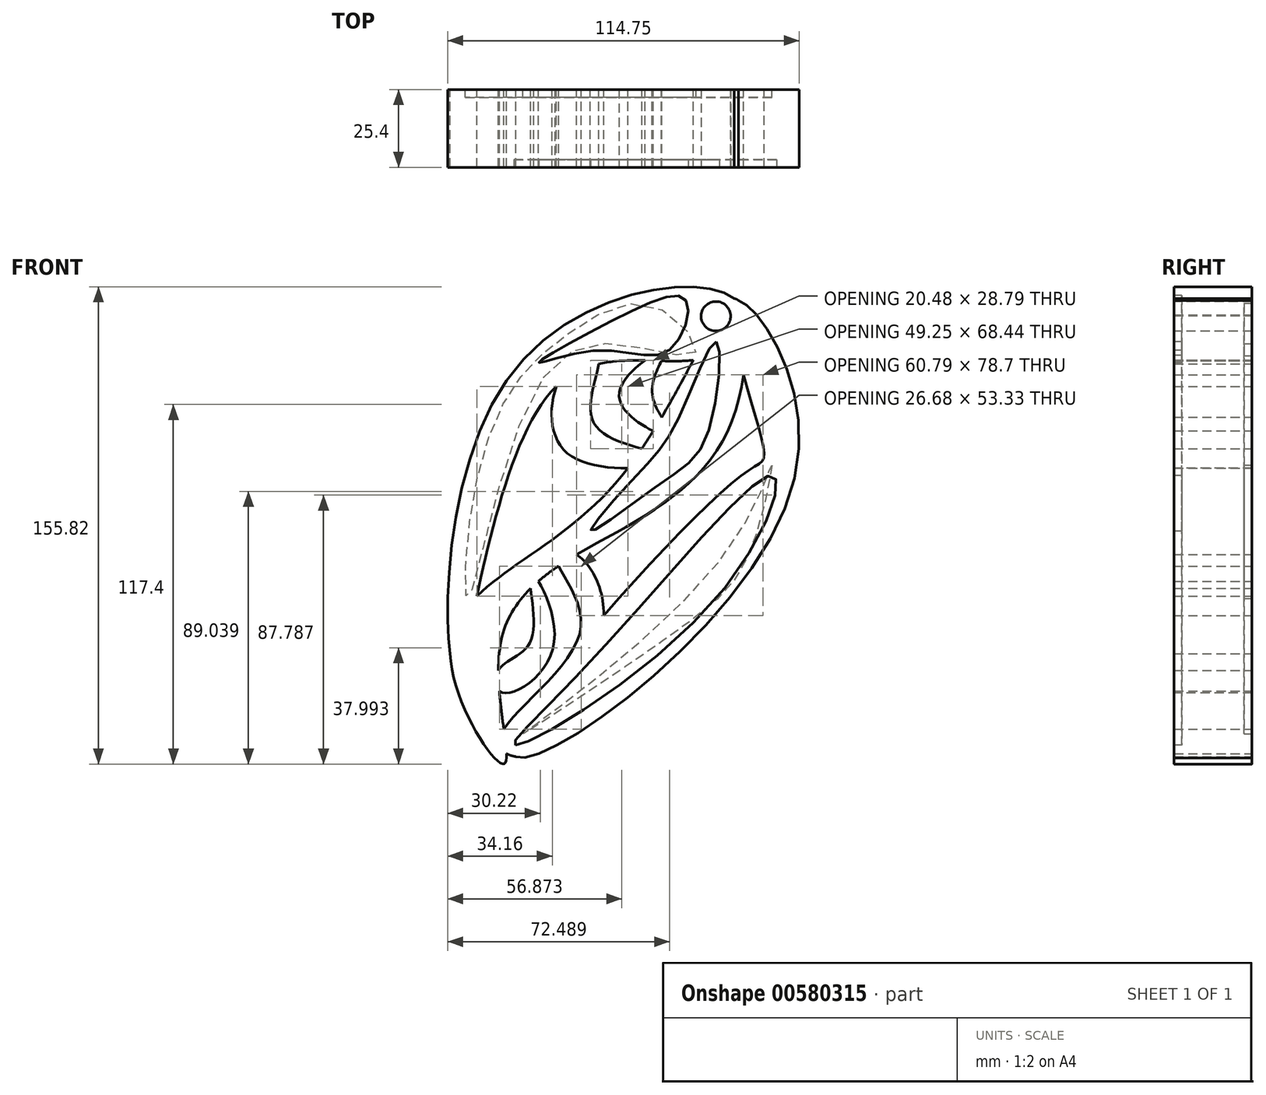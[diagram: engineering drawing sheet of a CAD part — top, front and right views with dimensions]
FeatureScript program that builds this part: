
annotation { "Feature Type Name" : "Feature", "Feature Type Description" : "" }
export const myFeature = defineFeature(function(context is Context, id is Id, definition is map)
    precondition{}
    {
        {
            var Q0;
            Q0=qCreatedBy(makeId("Front.planeOp"),FACE);
            var sketch = newSketch(context, id + "F0", { "sketchPlane" : qUnion([Q0])});
            skFitSpline(sketch, "E0", {"points": [v(37.9, 75.8) * mm, v(37.6, 37.9) * mm, v(0, 0) * mm, v(-38.5, -35.8) * mm, v(-37.6, -76.1) * mm, v(-55.04, -37.9) * mm, v(-3, 13.54) * mm, v(37.9, 75.8) * mm]});
            skSolve(sketch);
        }
        {
            var Q0;
            Q0 = qSketchRegion(id + "F0", true);
            extrude(context, id + "F1", {"entities" : qUnion([Q0]), "depth" : 25.4 * mm, "offsetDistance" : 25.4 * mm});
        }
        {
            var Q0;
            Q0=qCreatedBy(makeId("Front.planeOp"),FACE);
            var sketch = newSketch(context, id + "F2", { "sketchPlane" : qUnion([Q0])});
            skFitSpline(sketch, "E1", {"points": [v(-39.1, -45.12) * mm, v(-28.57, -35.2) * mm, v(-28.88, -14.14) * mm, v(-21.36, -37.3) * mm, v(-38.5, -52.64) * mm, v(-39.1, -45.12) * mm]});
            skSolve(sketch);
        }
        {
            var Q0;
            Q0 = qSketchRegion(id + "F2", true);
            extrude(context, id + "F3", {"entities" : qUnion([Q0]), "operationType" : NewBodyOperationType.ADD, "depth" : 25.4 * mm, "offsetDistance" : 25.4 * mm});
        }
        {
            var Q0;
            Q0=qCreatedBy(makeId("Front.planeOp"),FACE);
            var sketch = newSketch(context, id + "F4", { "sketchPlane" : qUnion([Q0])});
            skFitSpline(sketch, "E2", {"points": [v(-20.75, -8.42) * mm, v(-12.63, -32.49) * mm, v(-39.1, -68.58) * mm, v(-27.37, -72.8) * mm, v(-5.11, -24.66) * mm, v(-17.15, -6.32) * mm, v(-20.75, -8.42) * mm]});
            skSolve(sketch);
        }
        {
            var Q0;
            Q0 = qSketchRegion(id + "F4", true);
            extrude(context, id + "F5", {"entities" : qUnion([Q0]), "operationType" : NewBodyOperationType.ADD, "depth" : 25.4 * mm, "offsetDistance" : 25.4 * mm});
        }
        {
            var Q0;
            Q0=qCreatedBy(makeId("Front.planeOp"),FACE);
            var sketch = newSketch(context, id + "F6", { "sketchPlane" : qUnion([Q0])});
            skFitSpline(sketch, "E3", {"points": [v(38.8, 74.6) * mm, v(-35.5, 50.83) * mm, v(-52.94, -44.82) * mm, v(-21.06, 46.62) * mm, v(30.08, 57.15) * mm, v(38.8, 74.6) * mm]});
            skSolve(sketch);
        }
        {
            var Q0;
            Q0 = qSketchRegion(id + "F6", true);
            extrude(context, id + "F7", {"entities" : qUnion([Q0]), "operationType" : NewBodyOperationType.ADD, "depth" : 25.4 * mm, "offsetDistance" : 25.4 * mm});
        }
        {
            var Q0;
            Q0=qCreatedBy(makeId("Front.planeOp"),FACE);
            var sketch = newSketch(context, id + "F8", { "sketchPlane" : qUnion([Q0])});
            skCircle(sketch, "E4", {"center": v(30.98, 69.78) * mm, "radius": 4.44 * mm});
            skSolve(sketch);
        }
        {
            var Q0;
            Q0 = qSketchRegion(id + "F8", true);
            extrude(context, id + "F9", {"entities" : qUnion([Q0]), "operationType" : NewBodyOperationType.REMOVE, "oppositeDirection" : true, "depth" : 25.4 * mm, "offsetDistance" : 25.4 * mm});
        }
        {
            var Q0;
            Q0=makeQuery(id+"F7.boolean.opBoolean","MERGE",FACE,{"derivedFrom":[makeQuery(id+"F5.boolean.opBoolean","MERGE",FACE,{"derivedFrom":[makeQuery(id+"F3.boolean.opBoolean","MERGE",FACE,{"derivedFrom":[makeQuery(id+"F1.opExtrude","CAP_FACE",FACE,{"disambiguationData":[OSD([sQuery(id+"F0.wireOp",EDGE,"E0")])],"isStart":false}),makeQuery(id+"F3.opExtrude","CAP_FACE",FACE,{"disambiguationData":[OSD([sQuery(id+"F2.wireOp",EDGE,"E1")])],"isStart":false})]}),makeQuery(id+"F5.opExtrude","CAP_FACE",FACE,{"disambiguationData":[OSD([sQuery(id+"F4.wireOp",EDGE,"E2")])],"isStart":false})]}),makeQuery(id+"F7.opExtrude","CAP_FACE",FACE,{"disambiguationData":[OSD([sQuery(id+"F6.wireOp",EDGE,"E3")])],"isStart":false})]});
            var sketch = newSketch(context, id + "F10", { "sketchPlane" : qUnion([Q0])});
            skCircle(sketch, "E5", {"center": v(31.58, 70.08) * mm, "radius": 4.82 * mm});
            skSolve(sketch);
        }
        {
            var Q0;
            Q0 = qSketchRegion(id + "F10", true);
            extrude(context, id + "F11", {"entities" : qUnion([Q0]), "operationType" : NewBodyOperationType.REMOVE, "oppositeDirection" : true, "depth" : 25.4 * mm, "offsetDistance" : 25.4 * mm});
        }
        {
            var Q0;
            Q0=qCreatedBy(makeId("Front.planeOp"),FACE);
            var sketch = newSketch(context, id + "F12", { "sketchPlane" : qUnion([Q0])});
            skFitSpline(sketch, "E6", {"points": [v(37, 74.6) * mm, v(57.45, 18.05) * mm, v(-34.6, -72.8) * mm, v(40.6, 18.65) * mm, v(47.22, 26.17) * mm, v(37, 74.6) * mm]});
            skSolve(sketch);
        }
        {
            var Q0;
            Q0 = qSketchRegion(id + "F12", true);
            extrude(context, id + "F13", {"entities" : qUnion([Q0]), "operationType" : NewBodyOperationType.ADD, "depth" : 25.4 * mm, "offsetDistance" : 25.4 * mm});
        }
        {
            var Q0;
            Q0=qCreatedBy(makeId("Front.planeOp"),FACE);
            var sketch = newSketch(context, id + "F14", { "sketchPlane" : qUnion([Q0])});
            skFitSpline(sketch, "E7", {"points": [v(14.15, 58.06) * mm, v(10.77, 45.14) * mm, v(16.62, 31.3) * mm, v(0, 43.9) * mm, v(14.15, 58.06) * mm]});
            skSolve(sketch);
        }
        {
            var Q0;
            Q0 = qSketchRegion(id + "F14", true);
            extrude(context, id + "F15", {"entities" : qUnion([Q0]), "operationType" : NewBodyOperationType.ADD, "depth" : 25.4 * mm, "offsetDistance" : 25.4 * mm});
        }
        {
            var Q0;
            Q0=qCreatedBy(makeId("Front.planeOp"),FACE);
            var sketch = newSketch(context, id + "F16", { "sketchPlane" : qUnion([Q0])});
            skFitSpline(sketch, "E8", {"points": [v(-6.77, 57.14) * mm, v(-7.7, 34.37) * mm, v(17.23, 23.6) * mm, v(-16.62, 25.14) * mm, v(-15.08, 56.52) * mm, v(-6.77, 57.14) * mm]});
            skSolve(sketch);
        }
        {
            var Q0;
            Q0 = qSketchRegion(id + "F16", true);
            extrude(context, id + "F17", {"entities" : qUnion([Q0]), "operationType" : NewBodyOperationType.ADD, "depth" : 25.4 * mm, "offsetDistance" : 25.4 * mm});
        }
        {
            var Q0;
            Q0=makeQuery(id+"F17.boolean.opBoolean","MERGE",FACE,{"derivedFrom":[makeQuery(id+"F15.boolean.opBoolean","MERGE",FACE,{"derivedFrom":[makeQuery(id+"F13.boolean.opBoolean","MERGE",FACE,{"derivedFrom":[makeQuery(id+"F7.boolean.opBoolean","MERGE",FACE,{"derivedFrom":[makeQuery(id+"F5.boolean.opBoolean","MERGE",FACE,{"derivedFrom":[makeQuery(id+"F3.boolean.opBoolean","MERGE",FACE,{"derivedFrom":[makeQuery(id+"F1.opExtrude","CAP_FACE",FACE,{"disambiguationData":[OSD([sQuery(id+"F0.wireOp",EDGE,"E0")])],"isStart":false}),makeQuery(id+"F3.opExtrude","CAP_FACE",FACE,{"disambiguationData":[OSD([sQuery(id+"F2.wireOp",EDGE,"E1")])],"isStart":false})]}),makeQuery(id+"F5.opExtrude","CAP_FACE",FACE,{"disambiguationData":[OSD([sQuery(id+"F4.wireOp",EDGE,"E2")])],"isStart":false})]}),makeQuery(id+"F7.opExtrude","CAP_FACE",FACE,{"disambiguationData":[OSD([sQuery(id+"F6.wireOp",EDGE,"E3")])],"isStart":false})]}),makeQuery(id+"F13.opExtrude","CAP_FACE",FACE,{"disambiguationData":[OSD([sQuery(id+"F12.wireOp",EDGE,"E6")])],"isStart":false})]}),makeQuery(id+"F15.opExtrude","CAP_FACE",FACE,{"disambiguationData":[OSD([sQuery(id+"F14.wireOp",EDGE,"E7")])],"isStart":false})]}),makeQuery(id+"F17.opExtrude","CAP_FACE",FACE,{"disambiguationData":[OSD([sQuery(id+"F16.wireOp",EDGE,"E8")])],"isStart":false})]});
            var sketch = newSketch(context, id + "F18", { "sketchPlane" : qUnion([Q0])});
            skFitSpline(sketch, "E9", {"points": [v(-33.85, -69.94) * mm, v(-9.54, -42.87) * mm, v(49.85, 18.06) * mm, v(31.7, -21.94) * mm, v(-33.85, -69.94) * mm]});
            skSolve(sketch);
        }
        {
            var Q0;
            Q0 = qSketchRegion(id + "F18", true);
            extrude(context, id + "F19", {"entities" : qUnion([Q0]), "operationType" : NewBodyOperationType.REMOVE, "oppositeDirection" : true, "depth" : 2.54 * mm, "offsetDistance" : 25.4 * mm});
        }
        {
            var Q0;
            Q0=makeQuery(id+"F17.boolean.opBoolean","MERGE",FACE,{"derivedFrom":[makeQuery(id+"F15.boolean.opBoolean","MERGE",FACE,{"derivedFrom":[makeQuery(id+"F13.boolean.opBoolean","MERGE",FACE,{"derivedFrom":[makeQuery(id+"F7.boolean.opBoolean","MERGE",FACE,{"derivedFrom":[makeQuery(id+"F5.boolean.opBoolean","MERGE",FACE,{"derivedFrom":[makeQuery(id+"F3.boolean.opBoolean","MERGE",FACE,{"derivedFrom":[makeQuery(id+"F1.opExtrude","CAP_FACE",FACE,{"disambiguationData":[OSD([sQuery(id+"F0.wireOp",EDGE,"E0")])],"isStart":true}),makeQuery(id+"F3.opExtrude","CAP_FACE",FACE,{"disambiguationData":[OSD([sQuery(id+"F2.wireOp",EDGE,"E1")])],"isStart":true})]}),makeQuery(id+"F5.opExtrude","CAP_FACE",FACE,{"disambiguationData":[OSD([sQuery(id+"F4.wireOp",EDGE,"E2")])],"isStart":true})]}),makeQuery(id+"F7.opExtrude","CAP_FACE",FACE,{"disambiguationData":[OSD([sQuery(id+"F6.wireOp",EDGE,"E3")])],"isStart":true})]}),makeQuery(id+"F13.opExtrude","CAP_FACE",FACE,{"disambiguationData":[OSD([sQuery(id+"F12.wireOp",EDGE,"E6")])],"isStart":true})]}),makeQuery(id+"F15.opExtrude","CAP_FACE",FACE,{"disambiguationData":[OSD([sQuery(id+"F14.wireOp",EDGE,"E7")])],"isStart":true})]}),makeQuery(id+"F17.opExtrude","CAP_FACE",FACE,{"disambiguationData":[OSD([sQuery(id+"F16.wireOp",EDGE,"E8")])],"isStart":true})]});
            var sketch = newSketch(context, id + "F20", { "sketchPlane" : qUnion([Q0])});
            skFitSpline(sketch, "E10", {"points": [v(-24.92, 58.37) * mm, v(-2.77, 60.52) * mm, v(26.77, 46.98) * mm, v(49.23, -21.94) * mm, v(48.62, 4.21) * mm, v(35.7, 45.14) * mm, v(16.92, 64.22) * mm, v(-11.39, 73.45) * mm, v(-24.92, 58.37) * mm]});
            skSolve(sketch);
        }
        {
            var Q0;
            Q0 = qSketchRegion(id + "F20", true);
            extrude(context, id + "F21", {"entities" : qUnion([Q0]), "operationType" : NewBodyOperationType.REMOVE, "oppositeDirection" : true, "depth" : 2.54 * mm, "offsetDistance" : 25.4 * mm});
        }
        {
            var Q0;
            Q0=makeQuery(id+"F17.boolean.opBoolean","MERGE",FACE,{"derivedFrom":[makeQuery(id+"F15.boolean.opBoolean","MERGE",FACE,{"derivedFrom":[makeQuery(id+"F13.boolean.opBoolean","MERGE",FACE,{"derivedFrom":[makeQuery(id+"F7.boolean.opBoolean","MERGE",FACE,{"derivedFrom":[makeQuery(id+"F5.boolean.opBoolean","MERGE",FACE,{"derivedFrom":[makeQuery(id+"F3.boolean.opBoolean","MERGE",FACE,{"derivedFrom":[makeQuery(id+"F1.opExtrude","CAP_FACE",FACE,{"disambiguationData":[OSD([sQuery(id+"F0.wireOp",EDGE,"E0")])],"isStart":true}),makeQuery(id+"F3.opExtrude","CAP_FACE",FACE,{"disambiguationData":[OSD([sQuery(id+"F2.wireOp",EDGE,"E1")])],"isStart":true})]}),makeQuery(id+"F5.opExtrude","CAP_FACE",FACE,{"disambiguationData":[OSD([sQuery(id+"F4.wireOp",EDGE,"E2")])],"isStart":true})]}),makeQuery(id+"F7.opExtrude","CAP_FACE",FACE,{"disambiguationData":[OSD([sQuery(id+"F6.wireOp",EDGE,"E3")])],"isStart":true})]}),makeQuery(id+"F13.opExtrude","CAP_FACE",FACE,{"disambiguationData":[OSD([sQuery(id+"F12.wireOp",EDGE,"E6")])],"isStart":true})]}),makeQuery(id+"F15.opExtrude","CAP_FACE",FACE,{"disambiguationData":[OSD([sQuery(id+"F14.wireOp",EDGE,"E7")])],"isStart":true})]}),makeQuery(id+"F17.opExtrude","CAP_FACE",FACE,{"disambiguationData":[OSD([sQuery(id+"F16.wireOp",EDGE,"E8")])],"isStart":true})]});
            var sketch = newSketch(context, id + "F22", { "sketchPlane" : qUnion([Q0])});
            skFitSpline(sketch, "E11", {"points": [v(-49.85, 21.45) * mm, v(-43.39, -5.02) * mm, v(-18.77, -32.71) * mm, v(31.39, -66.25) * mm, v(-32.92, -9.63) * mm, v(-49.85, 21.45) * mm]});
            skSolve(sketch);
        }
        {
            var Q0;
            Q0 = qSketchRegion(id + "F22", true);
            extrude(context, id + "F23", {"entities" : qUnion([Q0]), "operationType" : NewBodyOperationType.REMOVE, "oppositeDirection" : true, "depth" : 2.54 * mm, "offsetDistance" : 25.4 * mm});
        }
        {
            var Q0;
            Q0=makeQuery(id+"F17.boolean.opBoolean","MERGE",FACE,{"derivedFrom":[makeQuery(id+"F15.boolean.opBoolean","MERGE",FACE,{"derivedFrom":[makeQuery(id+"F13.boolean.opBoolean","MERGE",FACE,{"derivedFrom":[makeQuery(id+"F7.boolean.opBoolean","MERGE",FACE,{"derivedFrom":[makeQuery(id+"F5.boolean.opBoolean","MERGE",FACE,{"derivedFrom":[makeQuery(id+"F3.boolean.opBoolean","MERGE",FACE,{"derivedFrom":[makeQuery(id+"F1.opExtrude","CAP_FACE",FACE,{"disambiguationData":[OSD([sQuery(id+"F0.wireOp",EDGE,"E0")])],"isStart":false}),makeQuery(id+"F3.opExtrude","CAP_FACE",FACE,{"disambiguationData":[OSD([sQuery(id+"F2.wireOp",EDGE,"E1")])],"isStart":false})]}),makeQuery(id+"F5.opExtrude","CAP_FACE",FACE,{"disambiguationData":[OSD([sQuery(id+"F4.wireOp",EDGE,"E2")])],"isStart":false})]}),makeQuery(id+"F7.opExtrude","CAP_FACE",FACE,{"disambiguationData":[OSD([sQuery(id+"F6.wireOp",EDGE,"E3")])],"isStart":false})]}),makeQuery(id+"F13.opExtrude","CAP_FACE",FACE,{"disambiguationData":[OSD([sQuery(id+"F12.wireOp",EDGE,"E6")])],"isStart":false})]}),makeQuery(id+"F15.opExtrude","CAP_FACE",FACE,{"disambiguationData":[OSD([sQuery(id+"F14.wireOp",EDGE,"E7")])],"isStart":false})]}),makeQuery(id+"F17.opExtrude","CAP_FACE",FACE,{"disambiguationData":[OSD([sQuery(id+"F16.wireOp",EDGE,"E8")])],"isStart":false})]});
            var sketch = newSketch(context, id + "F24", { "sketchPlane" : qUnion([Q0])});
            skFitSpline(sketch, "E12", {"points": [v(31.7, 61.75) * mm, v(19.39, 36.83) * mm, v(6.77, 19.3) * mm, v(-9.23, 0) * mm, v(13.23, 15.3) * mm, v(28.92, 31.9) * mm, v(31.7, 61.75) * mm]});
            skSolve(sketch);
        }
        {
            var Q0;
            Q0 = qSketchRegion(id + "F24", true);
            extrude(context, id + "F25", {"entities" : qUnion([Q0]), "operationType" : NewBodyOperationType.REMOVE, "oppositeDirection" : true, "depth" : 2.54 * mm, "offsetDistance" : 25.4 * mm});
        }
        {
            var Q0;
            Q0=makeQuery(id+"F17.boolean.opBoolean","MERGE",FACE,{"derivedFrom":[makeQuery(id+"F15.boolean.opBoolean","MERGE",FACE,{"derivedFrom":[makeQuery(id+"F13.boolean.opBoolean","MERGE",FACE,{"derivedFrom":[makeQuery(id+"F7.boolean.opBoolean","MERGE",FACE,{"derivedFrom":[makeQuery(id+"F5.boolean.opBoolean","MERGE",FACE,{"derivedFrom":[makeQuery(id+"F3.boolean.opBoolean","MERGE",FACE,{"derivedFrom":[makeQuery(id+"F1.opExtrude","CAP_FACE",FACE,{"disambiguationData":[OSD([sQuery(id+"F0.wireOp",EDGE,"E0")])],"isStart":false}),makeQuery(id+"F3.opExtrude","CAP_FACE",FACE,{"disambiguationData":[OSD([sQuery(id+"F2.wireOp",EDGE,"E1")])],"isStart":false})]}),makeQuery(id+"F5.opExtrude","CAP_FACE",FACE,{"disambiguationData":[OSD([sQuery(id+"F4.wireOp",EDGE,"E2")])],"isStart":false})]}),makeQuery(id+"F7.opExtrude","CAP_FACE",FACE,{"disambiguationData":[OSD([sQuery(id+"F6.wireOp",EDGE,"E3")])],"isStart":false})]}),makeQuery(id+"F13.opExtrude","CAP_FACE",FACE,{"disambiguationData":[OSD([sQuery(id+"F12.wireOp",EDGE,"E6")])],"isStart":false})]}),makeQuery(id+"F15.opExtrude","CAP_FACE",FACE,{"disambiguationData":[OSD([sQuery(id+"F14.wireOp",EDGE,"E7")])],"isStart":false})]}),makeQuery(id+"F17.opExtrude","CAP_FACE",FACE,{"disambiguationData":[OSD([sQuery(id+"F16.wireOp",EDGE,"E8")])],"isStart":false})]});
            var sketch = newSketch(context, id + "F26", { "sketchPlane" : qUnion([Q0])});
            skPoint(sketch, "E13.1.internal.snap0", {"position": v(26.77, 69.8) * mm});
            skFitSpline(sketch, "E13", {"points": [v(21.85, 75.3) * mm, v(0, 69.8) * mm, v(-26.16, 54.99) * mm, v(-6.66, 58.99) * mm, v(16.3, 58.99) * mm, v(21.85, 75.3) * mm]});
            skSolve(sketch);
        }
        {
            var Q0;
            Q0 = qSketchRegion(id + "F26", true);
            extrude(context, id + "F27", {"entities" : qUnion([Q0]), "operationType" : NewBodyOperationType.REMOVE, "oppositeDirection" : true, "depth" : 2.54 * mm, "offsetDistance" : 25.4 * mm});
        }
    });
